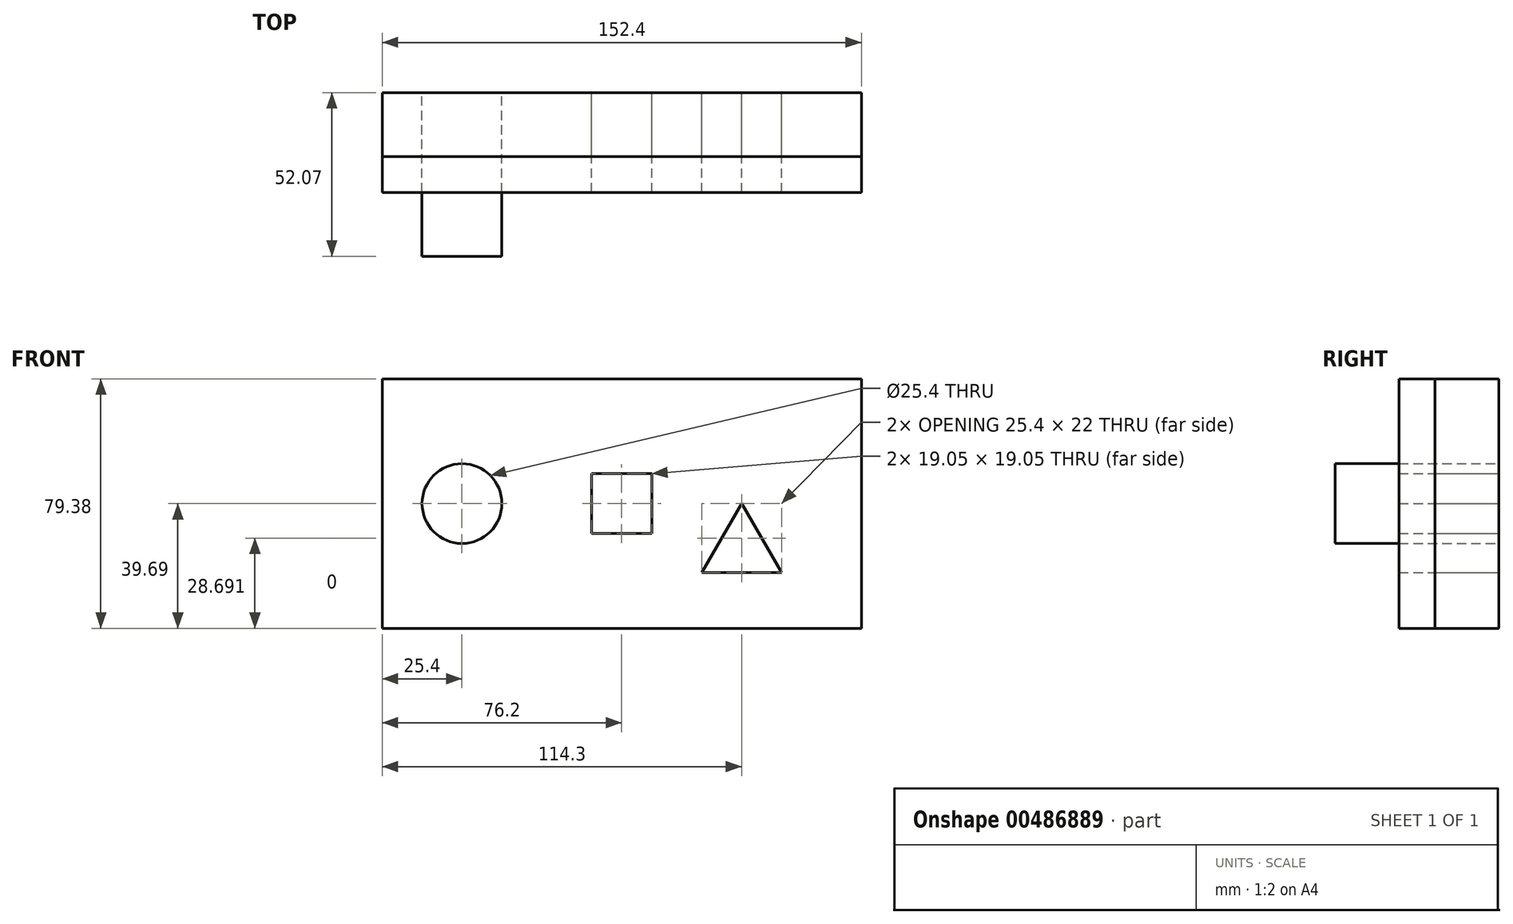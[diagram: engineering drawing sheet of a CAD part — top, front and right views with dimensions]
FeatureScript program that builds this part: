
annotation { "Feature Type Name" : "Feature", "Feature Type Description" : "" }
export const myFeature = defineFeature(function(context is Context, id is Id, definition is map)
    precondition{}
    {
        {
            var Q0;
            Q0=qCreatedBy(makeId("Front.planeOp"),FACE);
            var sketch = newSketch(context, id + "F0", { "sketchPlane" : qUnion([Q0])});
            skLineSegment(sketch, "E0", {"start": v(0, 0) * mm, "end": v(44.45, 0) * mm});
            skLineSegment(sketch, "E1", {"start": v(0, 0) * mm, "end": v(-31.75, 0) * mm});
            skLineSegment(sketch, "E2.bottom", {"start": v(44.45, 39.69) * mm, "end": v(-107.95, 39.69) * mm});
            skLineSegment(sketch, "E2.top", {"start": v(44.45, -39.69) * mm, "end": v(-107.95, -39.69) * mm});
            skLineSegment(sketch, "E2.left", {"start": v(44.45, 39.69) * mm, "end": v(44.45, -39.69) * mm});
            skLineSegment(sketch, "E2.right", {"start": v(-107.95, 39.69) * mm, "end": v(-107.95, -39.69) * mm});
            skPoint(sketch, "E2.middle", {"position": v(-31.75, 0) * mm});
            skLineSegment(sketch, "E3.bottom", {"start": v(-22.22, 9.53) * mm, "end": v(-41.27, 9.53) * mm});
            skLineSegment(sketch, "E3.top", {"start": v(-22.22, -9.53) * mm, "end": v(-41.27, -9.53) * mm});
            skLineSegment(sketch, "E3.left", {"start": v(-22.22, 9.53) * mm, "end": v(-22.22, -9.53) * mm});
            skLineSegment(sketch, "E3.right", {"start": v(-41.27, 9.53) * mm, "end": v(-41.27, -9.53) * mm});
            skLineSegment(sketch, "E4", {"start": v(-31.75, 0) * mm, "end": v(-82.55, 0) * mm});
            skCircle(sketch, "E5", {"center": v(-82.55, 0) * mm, "radius": 12.7 * mm});
            skLineSegment(sketch, "E6", {"start": v(0, 0) * mm, "end": v(6.35, 0) * mm});
            skLineSegment(sketch, "E7", {"start": v(6.35, 0) * mm, "end": v(-6.35, -22) * mm});
            skLineSegment(sketch, "E8", {"start": v(-6.35, -22) * mm, "end": v(19.05, -22) * mm});
            skLineSegment(sketch, "E9", {"start": v(19.05, -22) * mm, "end": v(6.35, 0) * mm});
            skSolve(sketch);
        }
        {
            var Q0;
            Q0=makeQuery(id+"F0.imprint","IMPRINT",FACE,{"disambiguationData":[TD([[makeQuery(id+"F0.imprint","IMPRINT",EDGE,{"derivedFrom":sQuery(id+"F0.wireOp",EDGE,"E5")}),1.0]])]});
            extrude(context, id + "F1", {"entities" : qUnion([Q0]), "depth" : 52.07 * mm});
        }
        {
            var Q0;
            Q0 = qSketchRegion(id + "F0", true);
            extrude(context, id + "F2", {"entities" : qUnion([Q0]), "operationType" : NewBodyOperationType.ADD, "depth" : 20.32 * mm});
        }
        {
            var Q0;
            Q0 = qSketchRegion(id + "F0", true);
            extrude(context, id + "F3", {"entities" : qUnion([Q0]), "depth" : 31.75 * mm});
        }
    });
